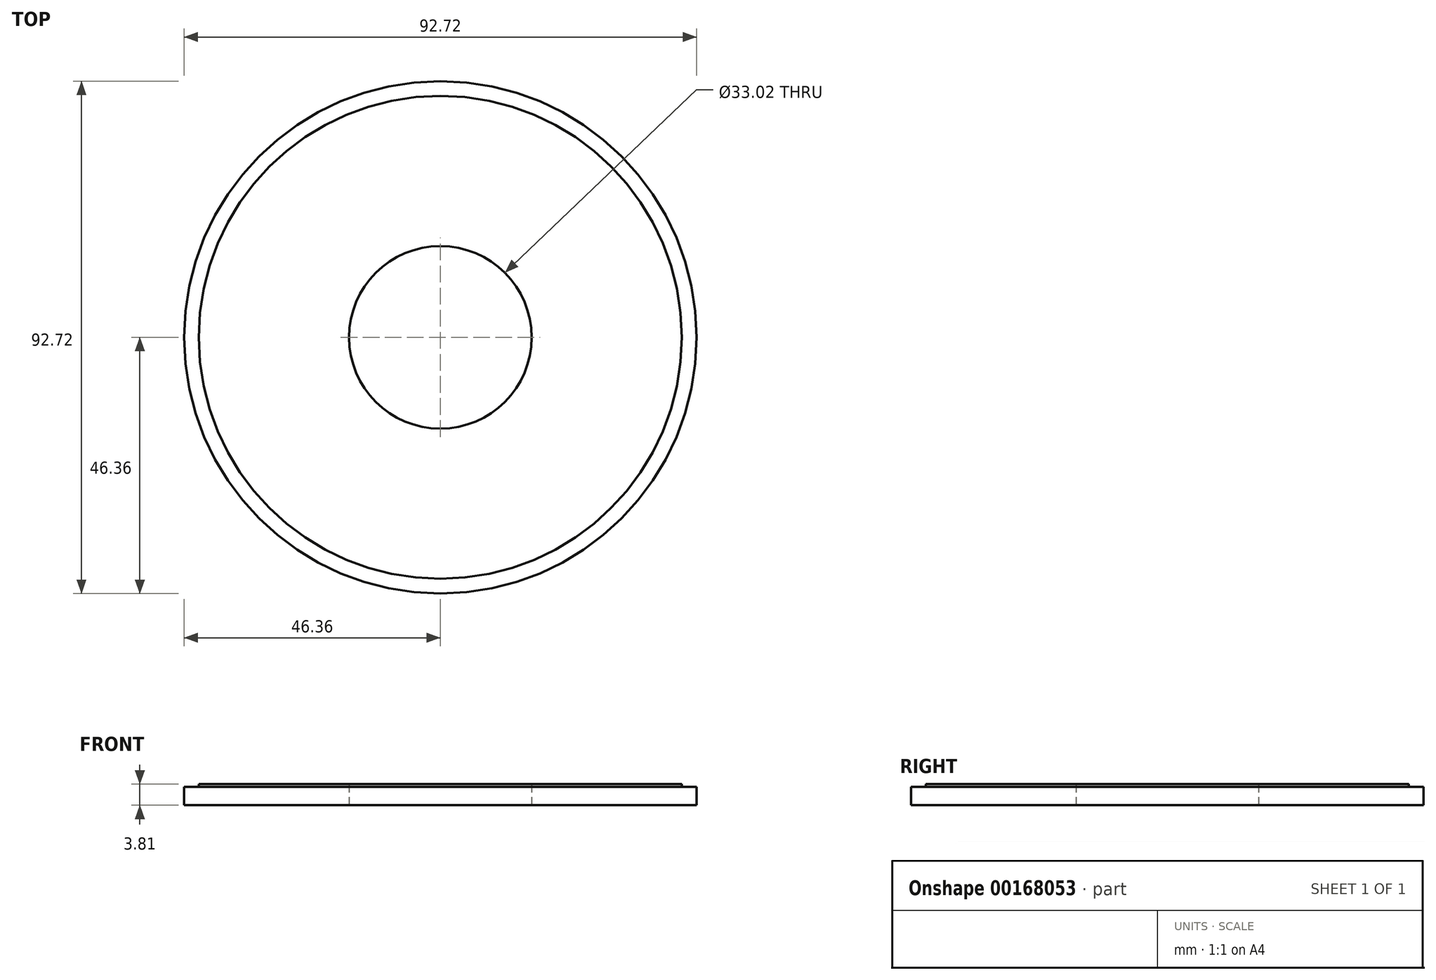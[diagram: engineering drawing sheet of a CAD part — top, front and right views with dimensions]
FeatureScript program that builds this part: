
annotation { "Feature Type Name" : "Feature", "Feature Type Description" : "" }
export const myFeature = defineFeature(function(context is Context, id is Id, definition is map)
    precondition{}
    {
        {
            var Q0;
            Q0=qCreatedBy(makeId("Top.planeOp"),FACE);
            var sketch = newSketch(context, id + "F0", { "sketchPlane" : qUnion([Q0])});
            skCircle(sketch, "E0", {"center": v(0, 0) * mm, "radius": 46.35 * mm});
            skCircle(sketch, "E1", {"center": v(0, 0) * mm, "radius": 16.51 * mm});
            skSolve(sketch);
        }
        {
            var Q0;
            Q0 = qSketchRegion(id + "F0", true);
            extrude(context, id + "F1", {"entities" : qUnion([Q0]), "depth" : 3.8 * mm});
        }
        {
            var Q0;
            Q0=makeQuery(id+"F1.opExtrude","CAP_FACE",FACE,{"disambiguationData":[OSD([sQuery(id+"F0.wireOp",EDGE,"E0"),sQuery(id+"F0.wireOp",EDGE,"E1")])],"isStart":false});
            var sketch = newSketch(context, id + "F2", { "sketchPlane" : qUnion([Q0])});
            skCircle(sketch, "E2.0", {"center": v(0, 0) * mm, "radius": 46.35 * mm});
            skCircle(sketch, "E3.0", {"center": v(0, 0) * mm, "radius": 43.69 * mm});
            skSolve(sketch);
        }
        {
            var Q0;
            Q0 = qSketchRegion(id + "F2", true);
            extrude(context, id + "F3", {"entities" : qUnion([Q0]), "operationType" : NewBodyOperationType.REMOVE, "oppositeDirection" : true, "depth" : 0.5 * mm});
        }
    });
